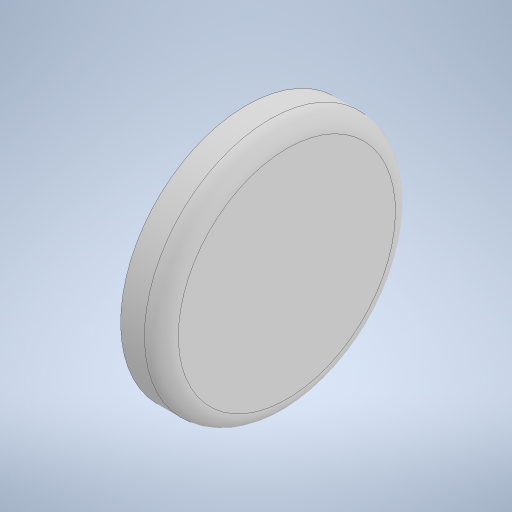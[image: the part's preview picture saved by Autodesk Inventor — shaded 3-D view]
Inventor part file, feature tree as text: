
AUTODESK INVENTOR PART (.ipt)
format: ipt  version: 2023 (Build 270158030, 158C)  size: 251,392 bytes
history: native  units: in
note: dims shown in document units (in); Inventor stores cm internally (conversion verified against a paired STEP export)
features: extrude x3, sketch x3, fillet x1
ambient origin geometry x8: Origin, YZ Plane, XZ Plane, XY Plane, X Axis, Y Axis, Z Axis, Center Point
bodies: Solid1 (feature_tree)
feature tree (7):
  extrude  "Extrusion1"  Depth=0.3in TaperAngle=0.0deg
  fillet  "Fillet1"  Radius=0.125in
  extrude  "Extrusion2"  Depth=0.15in
  extrude  "Extrusion3"  Depth=0.175in
  sketch  "Sketch1"  dims[d0=1.85in d1=0.3in d2=0.0in d3=0.125in]
  sketch  "Sketch2"  dims[d4=0.25in d5=0.15in]
  sketch  "Sketch3"  dims[d6=0.155in d7=0.0in d8=1.5in d9=0.25in d10=0.175in d11=0.0in]
